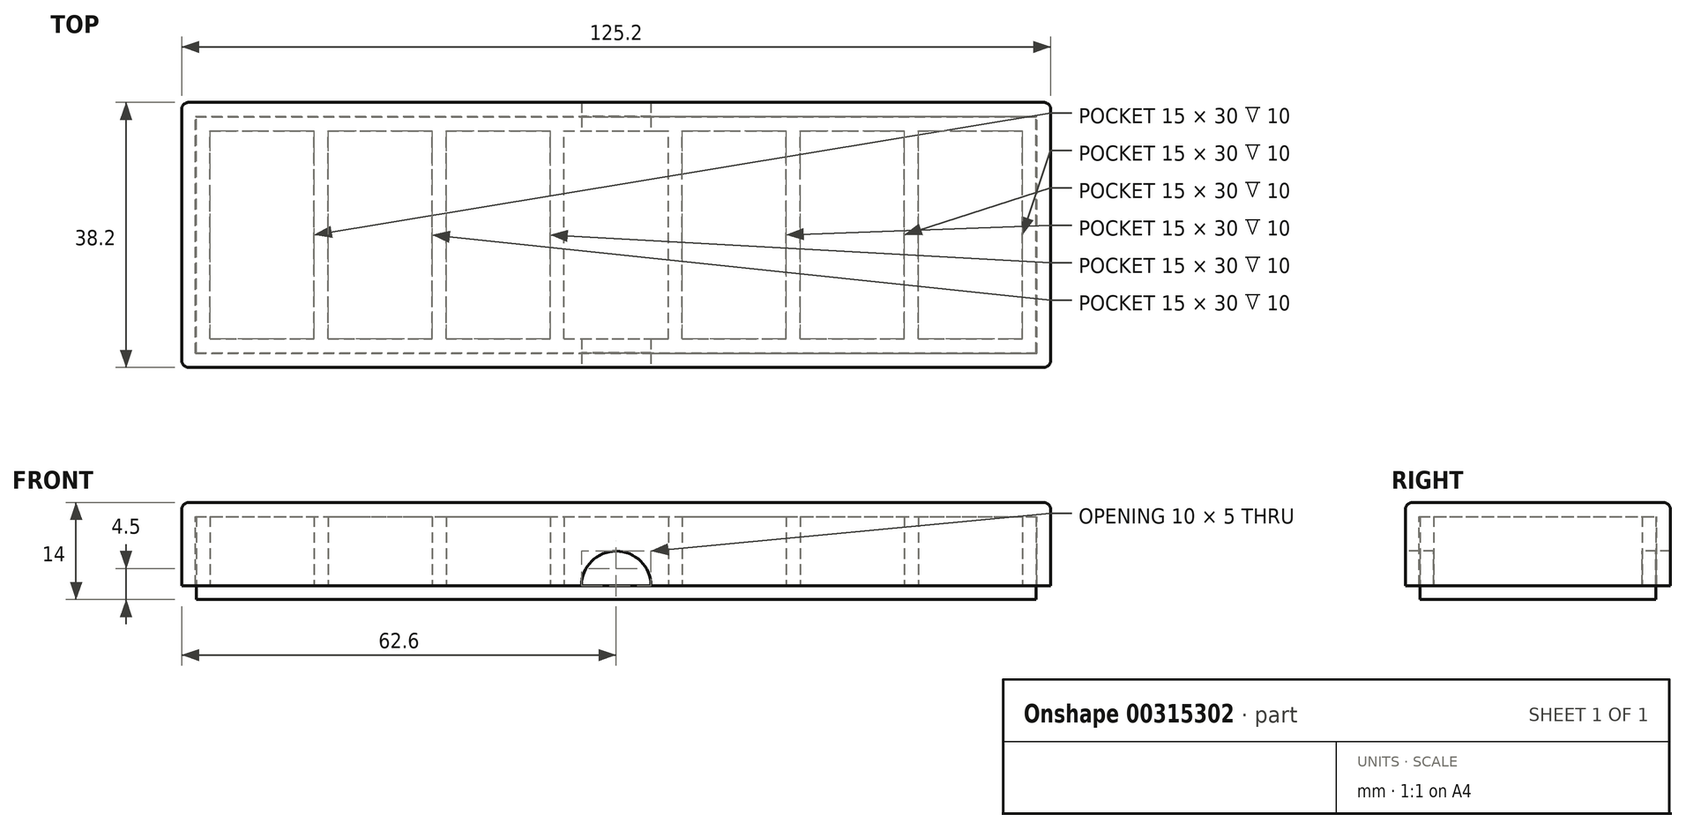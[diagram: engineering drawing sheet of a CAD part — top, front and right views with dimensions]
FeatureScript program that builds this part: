
annotation { "Feature Type Name" : "Feature", "Feature Type Description" : "" }
export const myFeature = defineFeature(function(context is Context, id is Id, definition is map)
    precondition{}
    {
        {
            var Q0;
            Q0=qCreatedBy(makeId("Top.planeOp"),FACE);
            var sketch = newSketch(context, id + "F0", { "sketchPlane" : qUnion([Q0])});
            skLineSegment(sketch, "E0.bottom", {"start": v(0, 0) * mm, "end": v(15, 0) * mm});
            skLineSegment(sketch, "E0.top", {"start": v(0, 30) * mm, "end": v(15, 30) * mm});
            skLineSegment(sketch, "E0.left", {"start": v(0, 0) * mm, "end": v(0, 30) * mm});
            skLineSegment(sketch, "E0.right", {"start": v(15, 0) * mm, "end": v(15, 30) * mm});
            skLineSegment(sketch, "E1.1.0.0", {"start": v(17, 30) * mm, "end": v(32, 30) * mm});
            skLineSegment(sketch, "E1.1.0.1", {"start": v(17, 0) * mm, "end": v(17, 30) * mm});
            skLineSegment(sketch, "E1.1.0.2", {"start": v(32, 0) * mm, "end": v(32, 30) * mm});
            skLineSegment(sketch, "E1.1.0.3", {"start": v(17, 0) * mm, "end": v(32, 0) * mm});
            skLineSegment(sketch, "E1.2.0.0", {"start": v(34, 30) * mm, "end": v(49, 30) * mm});
            skLineSegment(sketch, "E1.2.0.1", {"start": v(34, 0) * mm, "end": v(34, 30) * mm});
            skLineSegment(sketch, "E1.2.0.2", {"start": v(49, 0) * mm, "end": v(49, 30) * mm});
            skLineSegment(sketch, "E1.2.0.3", {"start": v(34, 0) * mm, "end": v(49, 0) * mm});
            skLineSegment(sketch, "E1.3.0.0", {"start": v(51, 30) * mm, "end": v(66, 30) * mm});
            skLineSegment(sketch, "E1.3.0.1", {"start": v(51, 0) * mm, "end": v(51, 30) * mm});
            skLineSegment(sketch, "E1.3.0.2", {"start": v(66, 0) * mm, "end": v(66, 30) * mm});
            skLineSegment(sketch, "E1.3.0.3", {"start": v(51, 0) * mm, "end": v(66, 0) * mm});
            skLineSegment(sketch, "E1.4.0.0", {"start": v(68, 30) * mm, "end": v(83, 30) * mm});
            skLineSegment(sketch, "E1.4.0.1", {"start": v(68, 0) * mm, "end": v(68, 30) * mm});
            skLineSegment(sketch, "E1.4.0.2", {"start": v(83, 0) * mm, "end": v(83, 30) * mm});
            skLineSegment(sketch, "E1.4.0.3", {"start": v(68, 0) * mm, "end": v(83, 0) * mm});
            skLineSegment(sketch, "E1.5.0.0", {"start": v(85, 30) * mm, "end": v(100, 30) * mm});
            skLineSegment(sketch, "E1.5.0.1", {"start": v(85, 0) * mm, "end": v(85, 30) * mm});
            skLineSegment(sketch, "E1.5.0.2", {"start": v(100, 0) * mm, "end": v(100, 30) * mm});
            skLineSegment(sketch, "E1.5.0.3", {"start": v(85, 0) * mm, "end": v(100, 0) * mm});
            skLineSegment(sketch, "E1.6.0.0", {"start": v(102, 30) * mm, "end": v(117, 30) * mm});
            skLineSegment(sketch, "E1.6.0.1", {"start": v(102, 0) * mm, "end": v(102, 30) * mm});
            skLineSegment(sketch, "E1.6.0.2", {"start": v(117, 0) * mm, "end": v(117, 30) * mm});
            skLineSegment(sketch, "E1.6.0.3", {"start": v(102, 0) * mm, "end": v(117, 0) * mm});
            skLineSegment(sketch, "E1.direction1", {"start": v(0, 0) * mm, "end": v(17, 0) * mm, "construction": true});
            skLineSegment(sketch, "E2.bottom", {"start": v(-2, -2) * mm, "end": v(119, -2) * mm});
            skLineSegment(sketch, "E2.top", {"start": v(-2, 32) * mm, "end": v(119, 32) * mm});
            skLineSegment(sketch, "E2.left", {"start": v(-2, -2) * mm, "end": v(-2, 32) * mm});
            skLineSegment(sketch, "E2.right", {"start": v(119, -2) * mm, "end": v(119, 32) * mm});
            skSolve(sketch);
        }
        {
            var Q0;
            Q0=makeQuery(id+"F0.imprint","IMPRINT",FACE,{"disambiguationData":[TD([[makeQuery(id+"F0.imprint","IMPRINT",EDGE,{"derivedFrom":sQuery(id+"F0.wireOp",EDGE,"E0.bottom")}),-1.0]])]});
            extrude(context, id + "F1", {"entities" : qUnion([Q0]), "depth" : 10 * mm});
        }
        {
            var Q0;
            Q0=makeQuery(id+"F0.imprint","IMPRINT",FACE,{"disambiguationData":[TD([[makeQuery(id+"F0.imprint","IMPRINT",EDGE,{"derivedFrom":sQuery(id+"F0.wireOp",EDGE,"E0.bottom")}),1.0]])]});
            var Q1;
            Q1=makeQuery(id+"F0.imprint","IMPRINT",FACE,{"disambiguationData":[TD([[makeQuery(id+"F0.imprint","IMPRINT",EDGE,{"derivedFrom":sQuery(id+"F0.wireOp",EDGE,"E1.1.0.0")}),-1.0]])]});
            var Q2;
            Q2=makeQuery(id+"F0.imprint","IMPRINT",FACE,{"disambiguationData":[TD([[makeQuery(id+"F0.imprint","IMPRINT",EDGE,{"derivedFrom":sQuery(id+"F0.wireOp",EDGE,"E1.2.0.0")}),-1.0]])]});
            var Q3;
            Q3=makeQuery(id+"F0.imprint","IMPRINT",FACE,{"disambiguationData":[TD([[makeQuery(id+"F0.imprint","IMPRINT",EDGE,{"derivedFrom":sQuery(id+"F0.wireOp",EDGE,"E1.3.0.0")}),-1.0]])]});
            var Q4;
            Q4=makeQuery(id+"F0.imprint","IMPRINT",FACE,{"disambiguationData":[TD([[makeQuery(id+"F0.imprint","IMPRINT",EDGE,{"derivedFrom":sQuery(id+"F0.wireOp",EDGE,"E1.4.0.0")}),-1.0]])]});
            var Q5;
            Q5=makeQuery(id+"F0.imprint","IMPRINT",FACE,{"disambiguationData":[TD([[makeQuery(id+"F0.imprint","IMPRINT",EDGE,{"derivedFrom":sQuery(id+"F0.wireOp",EDGE,"E1.5.0.0")}),-1.0]])]});
            var Q6;
            Q6=makeQuery(id+"F0.imprint","IMPRINT",FACE,{"disambiguationData":[TD([[makeQuery(id+"F0.imprint","IMPRINT",EDGE,{"derivedFrom":sQuery(id+"F0.wireOp",EDGE,"E1.6.0.0")}),-1.0]])]});
            var Q7;
            Q7=makeQuery(id+"F0.imprint","IMPRINT",FACE,{"disambiguationData":[TD([[makeQuery(id+"F0.imprint","IMPRINT",EDGE,{"derivedFrom":sQuery(id+"F0.wireOp",EDGE,"E0.bottom")}),-1.0]])]});
            extrude(context, id + "F2", {"entities" : qUnion([Q0, Q1, Q2, Q3, Q4, Q5, Q6, Q7]), "operationType" : NewBodyOperationType.ADD, "oppositeDirection" : true, "depth" : 2 * mm});
        }
        {
            var Q0;
            Q0=makeQuery(id+"F1.opExtrude","CAP_FACE",FACE,{"disambiguationData":[OSD([sQuery(id+"F0.wireOp",EDGE,"E0.bottom"),sQuery(id+"F0.wireOp",EDGE,"E0.top"),sQuery(id+"F0.wireOp",EDGE,"E0.left"),sQuery(id+"F0.wireOp",EDGE,"E0.right"),sQuery(id+"F0.wireOp",EDGE,"E1.1.0.0"),sQuery(id+"F0.wireOp",EDGE,"E1.1.0.1"),sQuery(id+"F0.wireOp",EDGE,"E1.1.0.2"),sQuery(id+"F0.wireOp",EDGE,"E1.1.0.3"),sQuery(id+"F0.wireOp",EDGE,"E1.2.0.0"),sQuery(id+"F0.wireOp",EDGE,"E1.2.0.1"),sQuery(id+"F0.wireOp",EDGE,"E1.2.0.2"),sQuery(id+"F0.wireOp",EDGE,"E1.2.0.3"),sQuery(id+"F0.wireOp",EDGE,"E1.3.0.0"),sQuery(id+"F0.wireOp",EDGE,"E1.3.0.1"),sQuery(id+"F0.wireOp",EDGE,"E1.3.0.2"),sQuery(id+"F0.wireOp",EDGE,"E1.3.0.3"),sQuery(id+"F0.wireOp",EDGE,"E1.4.0.0"),sQuery(id+"F0.wireOp",EDGE,"E1.4.0.1"),sQuery(id+"F0.wireOp",EDGE,"E1.4.0.2"),sQuery(id+"F0.wireOp",EDGE,"E1.4.0.3"),sQuery(id+"F0.wireOp",EDGE,"E1.5.0.0"),sQuery(id+"F0.wireOp",EDGE,"E1.5.0.1"),sQuery(id+"F0.wireOp",EDGE,"E1.5.0.2"),sQuery(id+"F0.wireOp",EDGE,"E1.5.0.3"),sQuery(id+"F0.wireOp",EDGE,"E1.6.0.0"),sQuery(id+"F0.wireOp",EDGE,"E1.6.0.1"),sQuery(id+"F0.wireOp",EDGE,"E1.6.0.2"),sQuery(id+"F0.wireOp",EDGE,"E1.6.0.3"),sQuery(id+"F0.wireOp",EDGE,"E2.bottom"),sQuery(id+"F0.wireOp",EDGE,"E2.top"),sQuery(id+"F0.wireOp",EDGE,"E2.left"),sQuery(id+"F0.wireOp",EDGE,"E2.right")])],"isStart":false});
            var sketch = newSketch(context, id + "F3", { "sketchPlane" : qUnion([Q0])});
            skLineSegment(sketch, "E3.0", {"start": v(-2, 32) * mm, "end": v(119, 32) * mm});
            skLineSegment(sketch, "E3.1", {"start": v(-2, -2) * mm, "end": v(-2, 32) * mm});
            skLineSegment(sketch, "E3.2", {"start": v(-2, -2) * mm, "end": v(119, -2) * mm});
            skLineSegment(sketch, "E3.3", {"start": v(119, -2) * mm, "end": v(119, 32) * mm});
            skLineSegment(sketch, "E4.0", {"start": v(-2.1, 32.1) * mm, "end": v(119.1, 32.1) * mm});
            skLineSegment(sketch, "E4.1", {"start": v(-2.1, -2.1) * mm, "end": v(-2.1, 32.1) * mm});
            skLineSegment(sketch, "E4.2", {"start": v(-2.1, -2.1) * mm, "end": v(119.1, -2.1) * mm});
            skLineSegment(sketch, "E4.3", {"start": v(119.1, -2.1) * mm, "end": v(119.1, 32.1) * mm});
            skLineSegment(sketch, "E5.0", {"start": v(-4.1, 34.1) * mm, "end": v(121.1, 34.1) * mm});
            skLineSegment(sketch, "E5.1", {"start": v(-4.1, -4.1) * mm, "end": v(-4.1, 34.1) * mm});
            skLineSegment(sketch, "E5.2", {"start": v(-4.1, -4.1) * mm, "end": v(121.1, -4.1) * mm});
            skLineSegment(sketch, "E5.3", {"start": v(121.1, -4.1) * mm, "end": v(121.1, 34.1) * mm});
            skSolve(sketch);
        }
        {
            var Q0;
            Q0=makeQuery(id+"F3.imprint","IMPRINT",FACE,{"disambiguationData":[TD([[makeQuery(id+"F3.imprint","IMPRINT",EDGE,{"derivedFrom":sQuery(id+"F3.wireOp",EDGE,"E3.0")}),1.0]])]});
            var Q1;
            Q1=makeQuery(id+"F3.imprint","IMPRINT",FACE,{"disambiguationData":[TD([[makeQuery(id+"F3.imprint","IMPRINT",EDGE,{"derivedFrom":sQuery(id+"F3.wireOp",EDGE,"E3.0")}),-1.0]])]});
            var Q2;
            Q2=makeQuery(id+"F3.imprint","IMPRINT",FACE,{"disambiguationData":[TD([[makeQuery(id+"F3.imprint","IMPRINT",EDGE,{"derivedFrom":makeQuery(id+"F1.opExtrude","CAP_EDGE",EDGE,{"disambiguationData":[OSD([sQuery(id+"F0.wireOp",EDGE,"E1.1.0.0")])],"isStart":false})}),-1.0]])]});
            var Q3;
            Q3=makeQuery(id+"F3.imprint","IMPRINT",FACE,{"disambiguationData":[TD([[makeQuery(id+"F3.imprint","IMPRINT",EDGE,{"derivedFrom":makeQuery(id+"F1.opExtrude","CAP_EDGE",EDGE,{"disambiguationData":[OSD([sQuery(id+"F0.wireOp",EDGE,"E0.bottom")])],"isStart":false})}),1.0]])]});
            var Q4;
            Q4=makeQuery(id+"F3.imprint","IMPRINT",FACE,{"disambiguationData":[TD([[makeQuery(id+"F3.imprint","IMPRINT",EDGE,{"derivedFrom":makeQuery(id+"F1.opExtrude","CAP_EDGE",EDGE,{"disambiguationData":[OSD([sQuery(id+"F0.wireOp",EDGE,"E1.2.0.0")])],"isStart":false})}),-1.0]])]});
            var Q5;
            Q5=makeQuery(id+"F3.imprint","IMPRINT",FACE,{"disambiguationData":[TD([[makeQuery(id+"F3.imprint","IMPRINT",EDGE,{"derivedFrom":makeQuery(id+"F1.opExtrude","CAP_EDGE",EDGE,{"disambiguationData":[OSD([sQuery(id+"F0.wireOp",EDGE,"E1.3.0.0")])],"isStart":false})}),-1.0]])]});
            var Q6;
            Q6=makeQuery(id+"F3.imprint","IMPRINT",FACE,{"disambiguationData":[TD([[makeQuery(id+"F3.imprint","IMPRINT",EDGE,{"derivedFrom":makeQuery(id+"F1.opExtrude","CAP_EDGE",EDGE,{"disambiguationData":[OSD([sQuery(id+"F0.wireOp",EDGE,"E1.4.0.0")])],"isStart":false})}),-1.0]])]});
            var Q7;
            Q7=makeQuery(id+"F3.imprint","IMPRINT",FACE,{"disambiguationData":[TD([[makeQuery(id+"F3.imprint","IMPRINT",EDGE,{"derivedFrom":makeQuery(id+"F1.opExtrude","CAP_EDGE",EDGE,{"disambiguationData":[OSD([sQuery(id+"F0.wireOp",EDGE,"E1.5.0.0")])],"isStart":false})}),-1.0]])]});
            var Q8;
            Q8=makeQuery(id+"F3.imprint","IMPRINT",FACE,{"disambiguationData":[TD([[makeQuery(id+"F3.imprint","IMPRINT",EDGE,{"derivedFrom":makeQuery(id+"F1.opExtrude","CAP_EDGE",EDGE,{"disambiguationData":[OSD([sQuery(id+"F0.wireOp",EDGE,"E1.6.0.0")])],"isStart":false})}),-1.0]])]});
            var Q9;
            Q9=makeQuery(id+"F3.imprint","IMPRINT",FACE,{"disambiguationData":[TD([[makeQuery(id+"F3.imprint","IMPRINT",EDGE,{"derivedFrom":sQuery(id+"F3.wireOp",EDGE,"E4.0")}),1.0]])]});
            extrude(context, id + "F4", {"entities" : qUnion([Q0, Q1, Q2, Q3, Q4, Q5, Q6, Q7, Q8, Q9]), "depth" : 2 * mm});
        }
        {
            var Q0;
            Q0=makeQuery(id+"F3.imprint","IMPRINT",FACE,{"disambiguationData":[TD([[makeQuery(id+"F3.imprint","IMPRINT",EDGE,{"derivedFrom":sQuery(id+"F3.wireOp",EDGE,"E4.0")}),1.0]])]});
            extrude(context, id + "F5", {"entities" : qUnion([Q0]), "operationType" : NewBodyOperationType.ADD, "oppositeDirection" : true, "depth" : 10 * mm});
        }
        {
            var Q0;
            Q0=makeQuery(id+"F4.opExtrude","CAP_FACE",FACE,{"disambiguationData":[OSD([sQuery(id+"F3.wireOp",EDGE,"E5.0"),sQuery(id+"F3.wireOp",EDGE,"E5.1"),sQuery(id+"F3.wireOp",EDGE,"E5.2"),sQuery(id+"F3.wireOp",EDGE,"E5.3")])],"isStart":false});
            var Q1;
            {var subQ0=sQuery(id+"F3.wireOp",EDGE,"E5.2");var subQ1=sQuery(id+"F3.wireOp",EDGE,"E5.1");Q1=makeQuery(id+"F5.boolean.opBoolean","MERGE",EDGE,{"derivedFrom":[makeQuery(id+"F4.opExtrude","SWEPT_EDGE",EDGE,{"disambiguationData":[OSD([subQ1,subQ0])]}),makeQuery(id+"F5.opExtrude","SWEPT_EDGE",EDGE,{"disambiguationData":[OSD([subQ1,subQ0])]})]});}
            var Q2;
            {var subQ0=sQuery(id+"F3.wireOp",EDGE,"E5.3");var subQ1=sQuery(id+"F3.wireOp",EDGE,"E5.2");Q2=makeQuery(id+"F5.boolean.opBoolean","MERGE",EDGE,{"derivedFrom":[makeQuery(id+"F4.opExtrude","SWEPT_EDGE",EDGE,{"disambiguationData":[OSD([subQ1,subQ0])]}),makeQuery(id+"F5.opExtrude","SWEPT_EDGE",EDGE,{"disambiguationData":[OSD([subQ1,subQ0])]})]});}
            var Q3;
            {var subQ0=sQuery(id+"F3.wireOp",EDGE,"E5.3");var subQ1=sQuery(id+"F3.wireOp",EDGE,"E5.0");Q3=makeQuery(id+"F5.boolean.opBoolean","MERGE",EDGE,{"derivedFrom":[makeQuery(id+"F4.opExtrude","SWEPT_EDGE",EDGE,{"disambiguationData":[OSD([subQ1,subQ0])]}),makeQuery(id+"F5.opExtrude","SWEPT_EDGE",EDGE,{"disambiguationData":[OSD([subQ1,subQ0])]})]});}
            var Q4;
            {var subQ0=sQuery(id+"F3.wireOp",EDGE,"E5.1");var subQ1=sQuery(id+"F3.wireOp",EDGE,"E5.0");Q4=makeQuery(id+"F5.boolean.opBoolean","MERGE",EDGE,{"derivedFrom":[makeQuery(id+"F4.opExtrude","SWEPT_EDGE",EDGE,{"disambiguationData":[OSD([subQ1,subQ0])]}),makeQuery(id+"F5.opExtrude","SWEPT_EDGE",EDGE,{"disambiguationData":[OSD([subQ1,subQ0])]})]});}
            fillet(context, id + "F6", {"entities" : qUnion([Q0, Q1, Q2, Q3, Q4]), "radius" : 1 * mm, "tangentPropagation" : true, "allowEdgeOverflow" : false});
        }
        {
            var Q0;
            {var subQ0=sQuery(id+"F3.wireOp",EDGE,"E5.2");Q0=makeQuery(id+"F5.boolean.opBoolean","MERGE",FACE,{"derivedFrom":[makeQuery(id+"F4.opExtrude","SWEPT_FACE",FACE,{"disambiguationData":[OSD([subQ0])]}),makeQuery(id+"F5.opExtrude","SWEPT_FACE",FACE,{"disambiguationData":[OSD([subQ0])]})]});}
            var sketch = newSketch(context, id + "F7", { "sketchPlane" : qUnion([Q0])});
            skCircle(sketch, "E6", {"center": v(58.5, 0) * mm, "radius": 5 * mm});
            skSolve(sketch);
        }
        {
            var Q0;
            {var subQ0=sQuery(id+"F7.wireOp",EDGE,"E6");var subQ1=makeQuery(id+"F5.opExtrude","CAP_EDGE",EDGE,{"disambiguationData":[OSD([sQuery(id+"F3.wireOp",EDGE,"E5.2")])],"isStart":false});var subQ2=makeQuery(id+"F7.imprint","INTERSECT",VERTEX,{"disambiguationData":[OD(0.0)],"derivedFrom":[subQ1,subQ0]});Q0=makeQuery(id+"F7.imprint","IMPRINT",FACE,{"disambiguationData":[TD([[makeQuery(id+"F7.imprint","IMPRINT",EDGE,{"disambiguationData":[TD([[subQ2,1.0]])],"derivedFrom":subQ0}),1.0]])]});}
            extrude(context, id + "F8", {"entities" : qUnion([Q0]), "operationType" : NewBodyOperationType.REMOVE, "endBound" : BoundingType.THROUGH_ALL, "oppositeDirection" : true, "depth" : 25 * mm});
        }
    });
